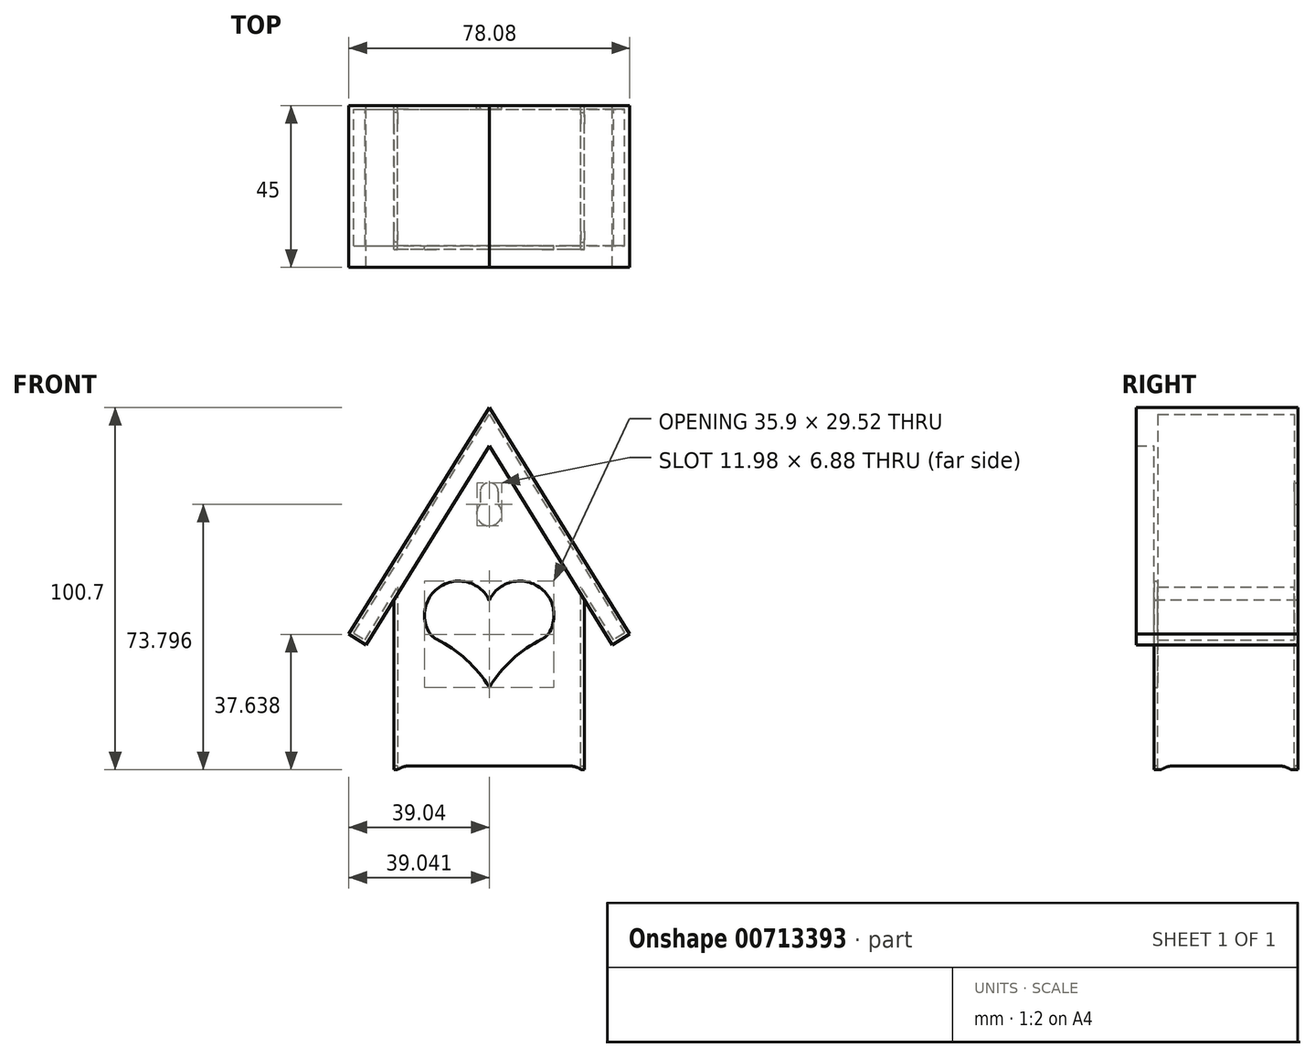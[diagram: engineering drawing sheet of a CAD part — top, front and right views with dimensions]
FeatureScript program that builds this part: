
annotation { "Feature Type Name" : "Feature", "Feature Type Description" : "" }
export const myFeature = defineFeature(function(context is Context, id is Id, definition is map)
    precondition{}
    {
        {
            var Q0;
            Q0=qCreatedBy(makeId("Front.planeOp"),FACE);
            var sketch = newSketch(context, id + "F0", { "sketchPlane" : qUnion([Q0])});
            skLineSegment(sketch, "E0", {"start": v(0, 90) * mm, "end": v(-34.25, 34.73) * mm});
            skLineSegment(sketch, "E1", {"start": v(34.25, 34.73) * mm, "end": v(0, 90) * mm});
            skLineSegment(sketch, "E2.bottom", {"start": v(-26.48, 0) * mm, "end": v(26.48, 0) * mm});
            skLineSegment(sketch, "E2.left", {"start": v(-26.48, 0) * mm, "end": v(-26.48, 47.26) * mm});
            skLineSegment(sketch, "E2.right", {"start": v(26.48, 0) * mm, "end": v(26.48, 47.26) * mm});
            skLineSegment(sketch, "E3", {"start": v(-34.25, 34.73) * mm, "end": v(-39.04, 37.7) * mm});
            skLineSegment(sketch, "E4", {"start": v(-39.04, 37.7) * mm, "end": v(0, 100.7) * mm});
            skLineSegment(sketch, "E5", {"start": v(0, 100.7) * mm, "end": v(39.04, 37.7) * mm});
            skLineSegment(sketch, "E6", {"start": v(39.04, 37.7) * mm, "end": v(34.25, 34.73) * mm});
            skArc(sketch, "E7", {"start": v(0, 47.18) * mm, "mid": v(-12.9, 51.35) * mm, "end": v(-16.84, 38.38) * mm});
            skArc(sketch, "E8", {"start": v(16.85, 38.4) * mm, "mid": v(12.89, 51.36) * mm, "end": v(0, 47.18) * mm});
            skArc(sketch, "E9", {"start": v(0, 22.88) * mm, "mid": v(-6.4, 30.62) * mm, "end": v(-14.68, 36.3) * mm});
            skPoint(sketch, "E10.orphan", {"position": v(-60, -17.13) * mm});
            skArc(sketch, "E11.trimOffspring", {"start": v(14.66, 36.3) * mm, "mid": v(6.37, 30.64) * mm, "end": v(0, 22.88) * mm});
            skPoint(sketch, "E12.start.orphan", {"position": v(60, -17.13) * mm});
            skPoint(sketch, "E13.visualSharp", {"position": v(-15.77, 36.82) * mm});
            skArc(sketch, "E13.filletArc", {"start": v(-16.84, 38.38) * mm, "mid": v(-15.91, 37.17) * mm, "end": v(-14.68, 36.3) * mm});
            skPoint(sketch, "E14.visualSharp", {"position": v(15.77, 36.82) * mm});
            skArc(sketch, "E14.filletArc", {"start": v(14.66, 36.3) * mm, "mid": v(15.92, 37.18) * mm, "end": v(16.85, 38.4) * mm});
            skLineSegment(sketch, "E15.left", {"start": v(-2.5, 77.29) * mm, "end": v(-2.5, 73.75) * mm});
            skLineSegment(sketch, "E15.right", {"start": v(2.5, 77.29) * mm, "end": v(2.5, 73.75) * mm});
            skArc(sketch, "E16.trimOffspring", {"start": v(2.5, 77.29) * mm, "mid": v(0, 79.79) * mm, "end": v(-2.5, 77.29) * mm});
            skArc(sketch, "E17.trimOffspring", {"start": v(-2.5, 73.75) * mm, "mid": v(0, 67.8) * mm, "end": v(2.5, 73.75) * mm});
            skLineSegment(sketch, "E18", {"start": v(-25.48, 48.87) * mm, "end": v(-25.48, 1) * mm});
            skLineSegment(sketch, "E19", {"start": v(-25.48, 1) * mm, "end": v(25.48, 1) * mm});
            skLineSegment(sketch, "E20", {"start": v(25.48, 1) * mm, "end": v(25.48, 48.87) * mm});
            skLineSegment(sketch, "E21", {"start": v(-25.48, 57.68) * mm, "end": v(0, 98.8) * mm});
            skLineSegment(sketch, "E22", {"start": v(0, 98.8) * mm, "end": v(25.48, 57.68) * mm});
            skLineSegment(sketch, "E23", {"start": v(25.48, 48.87) * mm, "end": v(25.48, 57.68) * mm});
            skLineSegment(sketch, "E24", {"start": v(-25.48, 48.87) * mm, "end": v(-25.48, 57.68) * mm});
            skLineSegment(sketch, "E25", {"start": v(-25.48, 57.68) * mm, "end": v(-37.66, 38.02) * mm});
            skLineSegment(sketch, "E26", {"start": v(-37.66, 38.02) * mm, "end": v(-34.57, 36.1) * mm});
            skLineSegment(sketch, "E27", {"start": v(-34.57, 36.1) * mm, "end": v(-25.48, 50.77) * mm});
            skLineSegment(sketch, "E28", {"start": v(25.48, 57.68) * mm, "end": v(37.66, 38.02) * mm});
            skLineSegment(sketch, "E29", {"start": v(37.66, 38.02) * mm, "end": v(34.57, 36.1) * mm});
            skLineSegment(sketch, "E30", {"start": v(34.57, 36.1) * mm, "end": v(25.48, 50.77) * mm});
            skLineSegment(sketch, "E31", {"start": v(-25.48, 1) * mm, "end": v(-25.48, 0) * mm});
            skLineSegment(sketch, "E32", {"start": v(25.48, 1) * mm, "end": v(25.48, 0) * mm});
            skArc(sketch, "E33", {"start": v(-130.4, -5.6) * mm, "mid": v(-142.55, -0.35) * mm, "end": v(-146.12, -13.08) * mm});
            skArc(sketch, "E34", {"start": v(-113.82, -12.6) * mm, "mid": v(-118.26, 0.06) * mm, "end": v(-130.4, -5.6) * mm});
            skArc(sketch, "E35", {"start": v(-130.15, -30.44) * mm, "mid": v(-136.26, -21.48) * mm, "end": v(-144.6, -14.55) * mm});
            skArc(sketch, "E36.trimOffspring", {"start": v(-116.14, -14.76) * mm, "mid": v(-124.8, -21.13) * mm, "end": v(-130.15, -30.44) * mm});
            skPoint(sketch, "E37.visualSharp", {"position": v(-145.32, -14.13) * mm});
            skArc(sketch, "E37.filletArc", {"start": v(-146.12, -13.08) * mm, "mid": v(-145.44, -13.9) * mm, "end": v(-144.6, -14.55) * mm});
            skPoint(sketch, "E38.visualSharp", {"position": v(-115, -14.27) * mm});
            skArc(sketch, "E38.filletArc", {"start": v(-116.14, -14.76) * mm, "mid": v(-114.8, -13.87) * mm, "end": v(-113.82, -12.6) * mm});
            skSolve(sketch);
        }
        {
            var Q0;
            Q0=makeQuery(id+"F0.imprint","IMPRINT",FACE,{"disambiguationData":[TD([[makeQuery(id+"F0.imprint","IMPRINT",EDGE,{"derivedFrom":sQuery(id+"F0.wireOp",EDGE,"E2.bottom")}),1.0]])]});
            var Q1;
            Q1=makeQuery(id+"F0.imprint","IMPRINT",FACE,{"disambiguationData":[TD([[makeQuery(id+"F0.imprint","IMPRINT",EDGE,{"derivedFrom":sQuery(id+"F0.wireOp",EDGE,"E15.left")}),1.0]])]});
            var Q2;
            Q2=makeQuery(id+"F0.imprint","IMPRINT",FACE,{"disambiguationData":[TD([[makeQuery(id+"F0.imprint","IMPRINT",EDGE,{"derivedFrom":sQuery(id+"F0.wireOp",EDGE,"E7")}),-1.0]])]});
            var Q3;
            Q3=makeQuery(id+"F0.imprint","IMPRINT",FACE,{"disambiguationData":[TD([[makeQuery(id+"F0.imprint","IMPRINT",EDGE,{"derivedFrom":sQuery(id+"F0.wireOp",EDGE,"E7")}),1.0]])]});
            var Q4;
            {var subQ1=sQuery(id+"F0.wireOp",EDGE,"E2.left");Q4=makeQuery(id+"F0.imprint","IMPRINT",FACE,{"disambiguationData":[TD([[makeQuery(id+"F0.imprint","IMPRINT",EDGE,{"derivedFrom":subQ1}),-1.0]])]});}
            var Q5;
            {var subQ1=sQuery(id+"F0.wireOp",EDGE,"E2.right");Q5=makeQuery(id+"F0.imprint","IMPRINT",FACE,{"disambiguationData":[TD([[makeQuery(id+"F0.imprint","IMPRINT",EDGE,{"derivedFrom":subQ1}),1.0]])]});}
            extrude(context, id + "F1", {"entities" : qUnion([Q0, Q1, Q2, Q3, Q4, Q5]), "depth" : 40 * mm, "offsetDistance" : 25 * mm});
        }
        {
            var Q0;
            {var subQ5=sQuery(id+"F0.wireOp",EDGE,"E3");Q0=makeQuery(id+"F0.imprint","IMPRINT",FACE,{"disambiguationData":[TD([[makeQuery(id+"F0.imprint","IMPRINT",EDGE,{"derivedFrom":subQ5}),-1.0]])]});}
            var Q1;
            Q1=makeQuery(id+"F0.imprint","IMPRINT",FACE,{"disambiguationData":[TD([[makeQuery(id+"F0.imprint","IMPRINT",EDGE,{"derivedFrom":sQuery(id+"F0.wireOp",EDGE,"E21")}),-1.0]])]});
            var Q2;
            {var subQ0=sQuery(id+"F0.wireOp",EDGE,"E25");Q2=makeQuery(id+"F0.imprint","IMPRINT",FACE,{"disambiguationData":[TD([[makeQuery(id+"F0.imprint","IMPRINT",EDGE,{"derivedFrom":subQ0}),1.0]])]});}
            var Q3;
            {var subQ0=sQuery(id+"F0.wireOp",EDGE,"E28");Q3=makeQuery(id+"F0.imprint","IMPRINT",FACE,{"disambiguationData":[TD([[makeQuery(id+"F0.imprint","IMPRINT",EDGE,{"derivedFrom":subQ0}),-1.0]])]});}
            extrude(context, id + "F2", {"entities" : qUnion([Q0, Q1, Q2, Q3]), "operationType" : NewBodyOperationType.ADD, "depth" : 45 * mm, "offsetDistance" : 25 * mm});
        }
        {
            var Q0;
            Q0=makeQuery(id+"F0.imprint","IMPRINT",FACE,{"disambiguationData":[TD([[makeQuery(id+"F0.imprint","IMPRINT",EDGE,{"derivedFrom":sQuery(id+"F0.wireOp",EDGE,"E15.left")}),1.0]])]});
            var Q1;
            Q1=makeQuery(id+"F0.imprint","IMPRINT",FACE,{"disambiguationData":[TD([[makeQuery(id+"F0.imprint","IMPRINT",EDGE,{"derivedFrom":sQuery(id+"F0.wireOp",EDGE,"E19")}),-1.0]])]});
            extrude(context, id + "F3", {"entities" : qUnion([Q0, Q1]), "operationType" : NewBodyOperationType.REMOVE, "depth" : 5 * mm, "offsetDistance" : 25 * mm});
        }
        {
            var Q0;
            Q0=makeQuery(id+"F0.imprint","IMPRINT",FACE,{"disambiguationData":[TD([[makeQuery(id+"F0.imprint","IMPRINT",EDGE,{"derivedFrom":sQuery(id+"F0.wireOp",EDGE,"E7")}),1.0]])]});
            extrude(context, id + "F4", {"entities" : qUnion([Q0]), "operationType" : NewBodyOperationType.REMOVE, "endBound" : BoundingType.THROUGH_ALL, "depth" : 25 * mm, "offsetDistance" : 25 * mm, "hasSecondDirection" : true, "secondDirectionOppositeDirection" : true, "secondDirectionDepth" : -1 * mm});
        }
        {
            var Q0;
            Q0=makeQuery(id+"F1.opExtrude","SWEPT_FACE",FACE,{"disambiguationData":[OSD([sQuery(id+"F0.wireOp",EDGE,"E2.bottom")])]});
            var sketch = newSketch(context, id + "F5", { "sketchPlane" : qUnion([Q0])});
            skCircle(sketch, "E39", {"center": v(0, 20) * mm, "radius": 2.5 * mm});
            skPoint(sketch, "E39.centerSnap0", {"position": v(-26.48, 20) * mm});
            skPoint(sketch, "E39.centerSnap1", {"position": v(0, 40) * mm});
            skSolve(sketch);
        }
        {
            var Q0;
            Q0=makeQuery(id+"F0.imprint","IMPRINT",FACE,{"disambiguationData":[TD([[makeQuery(id+"F0.imprint","IMPRINT",EDGE,{"derivedFrom":sQuery(id+"F0.wireOp",EDGE,"E7")}),-1.0]])]});
            var Q1;
            Q1=makeQuery(id+"F0.imprint","IMPRINT",FACE,{"disambiguationData":[TD([[makeQuery(id+"F0.imprint","IMPRINT",EDGE,{"derivedFrom":sQuery(id+"F0.wireOp",EDGE,"E21")}),-1.0]])]});
            var Q2;
            Q2=makeQuery(id+"F0.imprint","IMPRINT",FACE,{"disambiguationData":[TD([[makeQuery(id+"F0.imprint","IMPRINT",EDGE,{"derivedFrom":sQuery(id+"F0.wireOp",EDGE,"E15.left")}),1.0]])]});
            var Q3;
            {var subQ0=sQuery(id+"F0.wireOp",EDGE,"E25");Q3=makeQuery(id+"F0.imprint","IMPRINT",FACE,{"disambiguationData":[TD([[makeQuery(id+"F0.imprint","IMPRINT",EDGE,{"derivedFrom":subQ0}),1.0]])]});}
            var Q4;
            {var subQ0=sQuery(id+"F0.wireOp",EDGE,"E28");Q4=makeQuery(id+"F0.imprint","IMPRINT",FACE,{"disambiguationData":[TD([[makeQuery(id+"F0.imprint","IMPRINT",EDGE,{"derivedFrom":subQ0}),-1.0]])]});}
            var Q5;
            Q5=makeQuery(id+"F0.imprint","IMPRINT",FACE,{"disambiguationData":[TD([[makeQuery(id+"F0.imprint","IMPRINT",EDGE,{"derivedFrom":sQuery(id+"F0.wireOp",EDGE,"E19")}),-1.0]])]});
            extrude(context, id + "F6", {"entities" : qUnion([Q0, Q1, Q2, Q3, Q4, Q5]), "operationType" : NewBodyOperationType.REMOVE, "depth" : 39 * mm, "offsetDistance" : 25 * mm, "hasSecondDirection" : true, "secondDirectionOppositeDirection" : true, "secondDirectionDepth" : -1 * mm});
        }
        {
            var Q0;
            Q0=makeQuery(id+"F0.imprint","IMPRINT",FACE,{"disambiguationData":[TD([[makeQuery(id+"F0.imprint","IMPRINT",EDGE,{"derivedFrom":sQuery(id+"F0.wireOp",EDGE,"E19")}),-1.0]])]});
            extrude(context, id + "F7", {"entities" : qUnion([Q0]), "operationType" : NewBodyOperationType.REMOVE, "endBound" : BoundingType.THROUGH_ALL, "depth" : 25 * mm, "offsetDistance" : 25 * mm, "hasSecondDirection" : true, "secondDirectionOppositeDirection" : false, "secondDirectionDepth" : 1 * mm});
        }
        {
            var Q0;
            Q0=makeQuery(id+"F1.opExtrude","SWEPT_FACE",FACE,{"disambiguationData":[OSD([sQuery(id+"F0.wireOp",EDGE,"E2.left")])]});
            var sketch = newSketch(context, id + "F8", { "sketchPlane" : qUnion([Q0])});
            skLineSegment(sketch, "E40", {"start": v(5.07, 1) * mm, "end": v(34.93, 1) * mm});
            skLineSegment(sketch, "E41", {"start": v(37.43, 0.33) * mm, "end": v(38, 0) * mm});
            skPoint(sketch, "E42.orphan", {"position": v(0, 1) * mm});
            skLineSegment(sketch, "E43", {"start": v(2.57, 0.33) * mm, "end": v(2, 0) * mm});
            skPoint(sketch, "E44.visualSharp", {"position": v(3.73, 1) * mm});
            skArc(sketch, "E44.filletArc", {"start": v(5.07, 1) * mm, "mid": v(3.78, 0.83) * mm, "end": v(2.57, 0.33) * mm});
            skPoint(sketch, "E45.visualSharp", {"position": v(36.27, 1) * mm});
            skArc(sketch, "E45.filletArc", {"start": v(37.43, 0.33) * mm, "mid": v(36.22, 0.83) * mm, "end": v(34.93, 1) * mm});
            skSolve(sketch);
        }
        {
            var Q0;
            {var subQ0=sQuery(id+"F8.wireOp",EDGE,"E40");Q0=makeQuery(id+"F8.imprint","IMPRINT",FACE,{"disambiguationData":[TD([[makeQuery(id+"F8.imprint","IMPRINT",EDGE,{"derivedFrom":subQ0}),-1.0]])]});}
            extrude(context, id + "F9", {"entities" : qUnion([Q0]), "operationType" : NewBodyOperationType.REMOVE, "oppositeDirection" : true, "depth" : 25 * mm, "offsetDistance" : 25 * mm});
        }
        {
            var Q0;
            Q0=makeQuery(id+"F1.opExtrude","SWEPT_FACE",FACE,{"disambiguationData":[OSD([sQuery(id+"F0.wireOp",EDGE,"E2.right")])]});
            var sketch = newSketch(context, id + "F10", { "sketchPlane" : qUnion([Q0])});
            skLineSegment(sketch, "E46", {"start": v(-38, 0) * mm, "end": v(-37.43, 0.33) * mm});
            skLineSegment(sketch, "E47", {"start": v(-34.93, 1) * mm, "end": v(-5.07, 1) * mm});
            skLineSegment(sketch, "E48", {"start": v(-2.57, 0.33) * mm, "end": v(-2, 0) * mm});
            skPoint(sketch, "E49.visualSharp", {"position": v(-36.27, 1) * mm});
            skArc(sketch, "E49.filletArc", {"start": v(-34.93, 1) * mm, "mid": v(-36.22, 0.83) * mm, "end": v(-37.43, 0.33) * mm});
            skPoint(sketch, "E50.visualSharp", {"position": v(-3.73, 1) * mm});
            skArc(sketch, "E50.filletArc", {"start": v(-2.57, 0.33) * mm, "mid": v(-3.78, 0.83) * mm, "end": v(-5.07, 1) * mm});
            skSolve(sketch);
        }
        {
            var Q0;
            {var subQ0=sQuery(id+"F10.wireOp",EDGE,"E46");Q0=makeQuery(id+"F10.imprint","IMPRINT",FACE,{"disambiguationData":[TD([[makeQuery(id+"F10.imprint","IMPRINT",EDGE,{"derivedFrom":subQ0}),-1.0]])]});}
            extrude(context, id + "F11", {"entities" : qUnion([Q0]), "operationType" : NewBodyOperationType.REMOVE, "oppositeDirection" : true, "depth" : 25 * mm, "offsetDistance" : 25 * mm});
        }
        {
            var Q0;
            Q0=makeQuery(id+"F3.boolean.opBoolean","COPY",EDGE,{"derivedFrom":makeQuery(id+"F3.opExtrude","SWEPT_EDGE",EDGE,{"disambiguationData":[OSD([sQuery(id+"F0.wireOp",EDGE,"E19"),sQuery(id+"F0.wireOp",EDGE,"E20"),sQuery(id+"F0.wireOp",EDGE,"E32")])]})});
            var Q1;
            Q1=makeQuery(id+"F3.boolean.opBoolean","COPY",EDGE,{"derivedFrom":makeQuery(id+"F3.opExtrude","SWEPT_EDGE",EDGE,{"disambiguationData":[OSD([sQuery(id+"F0.wireOp",EDGE,"E18"),sQuery(id+"F0.wireOp",EDGE,"E19"),sQuery(id+"F0.wireOp",EDGE,"E31")])]})});
            var Q2;
            Q2=makeQuery(id+"F7.boolean.opBoolean","COPY",EDGE,{"derivedFrom":makeQuery(id+"F7.opExtrude","SWEPT_EDGE",EDGE,{"disambiguationData":[OSD([sQuery(id+"F0.wireOp",EDGE,"E19"),sQuery(id+"F0.wireOp",EDGE,"E20"),sQuery(id+"F0.wireOp",EDGE,"E32")])]})});
            var Q3;
            Q3=makeQuery(id+"F7.boolean.opBoolean","COPY",EDGE,{"derivedFrom":makeQuery(id+"F7.opExtrude","SWEPT_EDGE",EDGE,{"disambiguationData":[OSD([sQuery(id+"F0.wireOp",EDGE,"E18"),sQuery(id+"F0.wireOp",EDGE,"E19"),sQuery(id+"F0.wireOp",EDGE,"E31")])]})});
            fillet(context, id + "F12", {"entities" : qUnion([Q0, Q1, Q2, Q3]), "radius" : 5 * mm, "tangentPropagation" : true, "allowEdgeOverflow" : false});
        }
    });
